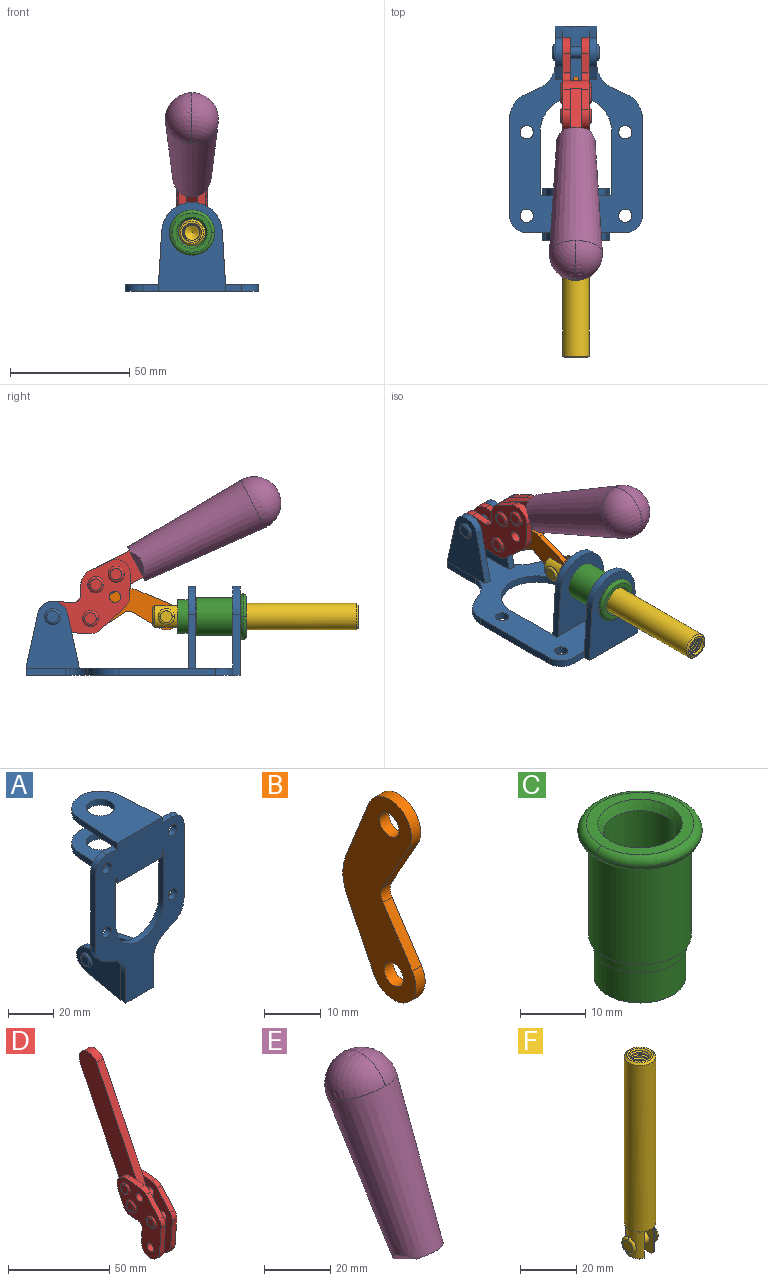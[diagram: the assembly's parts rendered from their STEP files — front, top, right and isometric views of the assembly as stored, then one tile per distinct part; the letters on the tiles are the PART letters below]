
ASSEMBLY  parts=6 mates=6
PART A: 55 faces, bbox 55.7x37.4x89.8 mm
  f0: torus R=2.41mm, axis (-1,0,0), area 15mm2, adj f11,f15,f25
  f1: torus R=2.41mm, axis (-1,0,0), area 15mm2, adj f10,f12,f22
  f2: cylinder r=2.78mm len=5.56mm, axis (0,-1,0), area 54.2mm2, adj f30,f54
  f3: cylinder r=14.99mm len=29.97mm, axis (0,-1,0), area 145.9mm2, adj f30,f49,f53,f54
  f4: cylinder r=2.78mm len=5.56mm, axis (0,-1,0), area 54.2mm2, adj f30,f54
  f5: cylinder r=2.78mm len=5.56mm, axis (0,-1,0), area 54.2mm2, adj f30,f54
  f6: cylinder r=2.78mm len=5.56mm, axis (0,-1,0), area 54.2mm2, adj f30,f54
  f7: cylinder r=6.35mm len=12.7mm, axis (0,0,1), area 123.6mm2, adj f27,f51
  f8: cylinder r=6.35mm len=12.7mm, axis (0,0,-1), area 124.7mm2, adj f21,f35
  f9: cylinder r=2.41mm len=11.18mm, axis (-1,0,0), area 169.4mm2, adj f16,f19
  f10: plane 4.83x4.83mm, normal (1,0,0), area 18.3mm2, adj f1,f12
  f11: plane 4.83x4.83mm, normal (-1,0,0), area 18.3mm2, adj f0,f15
  f12: torus R=2.41mm, axis (-1,0,0), area 15mm2, adj f1,f10,f22
  f13: cylinder r=6.35mm len=12.41mm, axis (1,0,0), area 53.4mm2, adj f18,f19,f22,f23
  f14: cylinder r=6.35mm len=12.41mm, axis (-1,0,0), area 53.4mm2, adj f16,f17,f24,f25
  f15: torus R=2.41mm, axis (-1,0,0), area 15mm2, adj f0,f11,f25
  f16: plane 27.86x22.35mm, normal (1,0,0), area 425.4mm2, adj f9,f14,f17,f24,f30
  f17: plane 22.86x4.97mm, normal (0,0.21,0.98), area 72.5mm2, adj f14,f16,f25,f30
  f18: plane 22.86x4.97mm, normal (0,0.21,0.98), area 72.5mm2, adj f13,f19,f22,f30
  f19: plane 27.86x22.35mm, normal (-1,0,0), area 425.4mm2, adj f9,f13,f18,f23,f30
  f20: cylinder r=12.7mm len=25.35mm, axis (0,0,-1), area 119.8mm2, adj f21,f34,f35,f36
  f21: plane 34.21x28.07mm, normal (0,0,-1), area 702.4mm2, adj f8,f20,f30,f34,f36
  f22: plane 27.96x22.45mm, normal (1,0,0), area 407.2mm2, adj f1,f12,f13,f18,f23,f30,f42,f43
  f23: plane 22.86x4.97mm, normal (0,0.21,-0.98), area 72.5mm2, adj f13,f19,f22,f44
  f24: plane 22.86x4.97mm, normal (0,0.21,-0.98), area 72.5mm2, adj f14,f16,f25,f44
  f25: plane 27.86x22.35mm, normal (-1,0,0), area 407.1mm2, adj f0,f14,f15,f17,f24,f30,f45,f46
  f26: plane 3.1x0.95mm, normal (0,0,-1), area 2.7mm2, adj f30,f49,f50,f54
  f27: plane 34.21x28.07mm, normal (0,0,1), area 702.4mm2, adj f7,f28,f30,f50,f52
  f28: cylinder r=12.7mm len=25.35mm, axis (0,0,1), area 118.8mm2, adj f27,f50,f51,f52
  f29: plane 3.1x0.95mm, normal (0,0,-1), area 2.7mm2, adj f30,f52,f53,f54
  f30: plane 86.54x55.63mm, normal (0,1,0), area 2362.9mm2, adj f2,f3,f4,f5,f6,f16,f17,f18
  f31: plane 40.56x3.1mm, normal (-1,0,0), area 125.7mm2, adj f30,f32,f48,f54
  f32: cylinder r=7.11mm len=7.11mm, axis (0,-1,0), area 34.6mm2, adj f30,f31,f33,f54
  f33: plane 6.67x3.1mm, normal (0,0,1), area 20.4mm2, adj f30,f32,f34,f54
  f34: plane 25.39x3.13mm, normal (-1,0.06,0), area 79.5mm2, adj f20,f21,f33,f35,f54
  f35: plane 37.31x28.45mm, normal (0,0,1), area 789.9mm2, adj f8,f20,f34,f36,f54
  f36: plane 25.39x3.13mm, normal (1,0.06,0), area 79.5mm2, adj f20,f21,f35,f37,f54
  f37: plane 6.67x3.1mm, normal (0,0,1), area 20.4mm2, adj f30,f36,f38,f54
  f38: cylinder r=7.11mm len=7.11mm, axis (0,-1,0), area 34.6mm2, adj f30,f37,f39,f54
  f39: plane 40.56x3.1mm, normal (1,0,0), area 125.7mm2, adj f30,f38,f40,f54
  f40: cylinder r=11.18mm len=10.16mm, axis (0,-1,0), area 39.5mm2, adj f30,f39,f41,f54
  f41: plane 6.09x3.1mm, normal (0.42,0,-0.91), area 20.8mm2, adj f30,f40,f42,f54
  f42: cylinder r=11.18mm len=9.41mm, axis (0,-1,0), area 37.2mm2, adj f22,f30,f41,f43,f54
  f43: plane 16.5x3.1mm, normal (1,0,0), area 51.1mm2, adj f22,f42,f44,f54
  f44: plane 17.37x3.1mm, normal (0,0,-1), area 53.8mm2, adj f23,f24,f30,f43,f45,f54
  f45: plane 16.5x3.1mm, normal (-1,0,0), area 51.1mm2, adj f25,f44,f46,f54
  f46: cylinder r=11.18mm len=9.41mm, axis (0,-1,0), area 37.2mm2, adj f25,f30,f45,f47,f54
  f47: plane 6.09x3.1mm, normal (-0.42,0,-0.91), area 20.8mm2, adj f30,f46,f48,f54
  f48: cylinder r=11.18mm len=10.16mm, axis (0,-1,0), area 39.5mm2, adj f30,f31,f47,f54
  f49: plane 26.54x3.1mm, normal (-1,0,0), area 82.3mm2, adj f3,f26,f30,f54
  f50: plane 25.39x3.1mm, normal (1,0.06,0), area 78.8mm2, adj f26,f27,f28,f51,f54
  f51: plane 37.31x28.45mm, normal (0,0,-1), area 789.9mm2, adj f7,f28,f50,f52,f54
  f52: plane 25.39x3.1mm, normal (-1,0.06,0), area 78.8mm2, adj f27,f28,f29,f51,f54
  f53: plane 26.54x3.1mm, normal (1,0,0), area 82.3mm2, adj f3,f29,f30,f54
  f54: plane 89.66x55.63mm, normal (0,-1,0), area 2678.5mm2, adj f2,f3,f4,f5,f6,f26,f29,f31
PART B: 12 faces, bbox 2.3x18.2x42.8 mm
  f0: cylinder r=2.4mm len=4.8mm, axis (1,0,0), area 34.9mm2, adj f4,f11
  f1: cylinder r=10.41mm len=8.47mm, axis (1,0,0), area 20.2mm2, adj f4,f9,f10,f11
  f2: cylinder r=3.05mm len=3.16mm, axis (1,0,0), area 7.7mm2, adj f4,f6,f7,f11
  f3: cylinder r=2.4mm len=4.8mm, axis (1,0,0), area 34.9mm2, adj f4,f11
  f4: plane 42.81x18.23mm, normal (-1,0,0), area 414.1mm2, adj f0,f1,f2,f3,f5,f6,f7,f8
  f5: cylinder r=5.54mm len=10.67mm, axis (1,0,0), area 41.8mm2, adj f4,f6,f10,f11
  f6: plane 11.66x6.53mm, normal (0,-0.87,-0.49), area 30.9mm2, adj f2,f4,f5,f11
  f7: plane 11.17x7.33mm, normal (0,-0.84,0.55), area 30.9mm2, adj f2,f4,f8,f11
  f8: cylinder r=5.54mm len=10.51mm, axis (1,0,0), area 41.8mm2, adj f4,f7,f9,f11
  f9: plane 13.67x6.67mm, normal (0,0.9,-0.44), area 35.1mm2, adj f1,f4,f8,f11
  f10: plane 14.1x5.7mm, normal (0,0.93,0.37), area 35.1mm2, adj f1,f4,f5,f11
  f11: plane 42.81x18.23mm, normal (1,0,0), area 414.1mm2, adj f0,f1,f2,f3,f5,f6,f7,f8
PART C: 15 faces, bbox 20.6x20.6x28.7 mm
  f0: torus R=8.26mm, axis (0,0,1), area 56.8mm2, adj f1,f10,f12
  f1: torus R=8.26mm, axis (0,0,1), area 56.8mm2, adj f0,f6,f13
  f2: cylinder r=5.59mm len=25.91mm, axis (0,0,1), area 909.6mm2, adj f3,f4
  f3: cone r=6.86mm half-angle=45deg, axis (0,0,-1), area 70.2mm2, adj f2,f14
  f4: cone r=6.47mm half-angle=30deg, axis (0,0,1), area 66.7mm2, adj f2,f13
  f5: cylinder r=7.04mm len=14.07mm, axis (0,0,1), area 252.6mm2, adj f11,f14
  f6: torus R=8.26mm, axis (0,0,1), area 56.8mm2, adj f1,f12,f13
  f7: cylinder r=7.16mm len=14.33mm, axis (0,0,1), area 91.5mm2, adj f9,f11
  f8: cylinder r=7.86mm len=18.42mm, axis (0,0,1), area 909.6mm2, adj f9,f10
  f9: plane 15.72x15.72mm, normal (0,0,-1), area 33mm2, adj f7,f8
  f10: plane 16.51x16.51mm, normal (0,0,-1), area 19.9mm2, adj f0,f8,f12
  f11: plane 14.33x14.33mm, normal (0,0,-1), area 5.7mm2, adj f5,f7
  f12: torus R=8.26mm, axis (0,0,1), area 56.8mm2, adj f0,f6,f10
  f13: plane 16.51x16.51mm, normal (0,0,1), area 82.7mm2, adj f1,f4,f6
  f14: plane 14.07x14.07mm, normal (0,0,-1), area 7.8mm2, adj f3,f5
PART D: 59 faces, bbox 12.9x60.2x99.6 mm
  f0: torus R=2.39mm, axis (-1,0,0), area 14.9mm2, adj f20,f43,f51
  f1: torus R=2.39mm, axis (-1,0,0), area 14.9mm2, adj f19,f42,f51
  f2: torus R=2.39mm, axis (-1,0,0), area 14.9mm2, adj f18,f35,f51
  f3: torus R=2.39mm, axis (-1,0,0), area 14.9mm2, adj f14,f17,f23
  f4: torus R=2.39mm, axis (-1,0,0), area 14.9mm2, adj f13,f16,f23
  f5: torus R=2.39mm, axis (-1,0,0), area 14.9mm2, adj f12,f15,f23
  f6: cylinder r=2.39mm len=4.78mm, axis (1,0,0), area 46.5mm2, adj f48,f50,f51
  f7: cylinder r=2.39mm len=4.78mm, axis (1,0,0), area 46.5mm2, adj f50,f51
  f8: cylinder r=6.35mm len=12.68mm, axis (1,0,0), area 61.8mm2, adj f38,f39,f50,f51
  f9: cylinder r=2.39mm len=4.78mm, axis (-1,0,0), area 70.5mm2, adj f46,f50
  f10: cylinder r=2.39mm len=4.78mm, axis (-1,0,0), area 46.5mm2, adj f23,f45,f46
  f11: cylinder r=2.39mm len=4.78mm, axis (-1,0,0), area 46.5mm2, adj f23,f46
  f12: plane 4.78x4.78mm, normal (1,0,0), area 17.9mm2, adj f5,f15
  f13: plane 4.78x4.78mm, normal (1,0,0), area 17.9mm2, adj f4,f16
  f14: plane 4.78x4.78mm, normal (1,0,0), area 17.9mm2, adj f3,f17
  f15: torus R=2.39mm, axis (-1,0,0), area 14.9mm2, adj f5,f12,f23
  f16: torus R=2.39mm, axis (-1,0,0), area 14.9mm2, adj f4,f13,f23
  f17: torus R=2.39mm, axis (-1,0,0), area 14.9mm2, adj f3,f14,f23
  f18: plane 4.78x4.78mm, normal (-1,0,0), area 17.9mm2, adj f2,f35
  f19: plane 4.78x4.78mm, normal (-1,0,0), area 17.9mm2, adj f1,f42
  f20: plane 4.78x4.78mm, normal (-1,0,0), area 17.9mm2, adj f0,f43
  f21: plane 2.26x0.2mm, normal (1,0,0), area 0.2mm2, adj f31,f44
  f22: plane 2.26x0.2mm, normal (-1,0,0), area 0.2mm2, adj f41,f44
  f23: plane 39.37x30.77mm, normal (1,0,0), area 565.5mm2, adj f3,f4,f5,f10,f11,f15,f16,f17
  f24: cylinder r=6.1mm len=4.15mm, axis (-1,0,0), area 14.7mm2, adj f23,f25,f32,f46
  f25: plane 10.25x9.01mm, normal (0,-0.75,0.66), area 42.3mm2, adj f23,f24,f26,f46
  f26: cylinder r=6.35mm len=4.64mm, axis (-1,0,0), area 15.6mm2, adj f23,f25,f27,f46
  f27: plane 15.84x3.1mm, normal (0,-1,-0.07), area 49.2mm2, adj f23,f26,f28,f46
  f28: cylinder r=6.35mm len=12.68mm, axis (-1,0,0), area 61.8mm2, adj f23,f27,f29,f46
  f29: plane 8.11x3.1mm, normal (0,1,0.07), area 25.2mm2, adj f23,f28,f30,f46
  f30: cylinder r=3.05mm len=3.25mm, axis (-1,0,0), area 14.8mm2, adj f23,f29,f31,f46
  f31: plane 5.99x3.1mm, normal (0,0.07,-1), area 18.6mm2, adj f21,f23,f30,f44,f46
  f32: plane 9.5x3.1mm, normal (0,-0.07,1), area 29.5mm2, adj f23,f24,f33,f46,f47
  f33: cylinder r=6.1mm len=8.63mm, axis (-1,0,0), area 39.1mm2, adj f23,f32,f34,f47
  f34: plane 8.65x3.96mm, normal (0,0.91,-0.42), area 29.5mm2, adj f23,f33,f44,f47
  f35: torus R=2.39mm, axis (-1,0,0), area 14.9mm2, adj f2,f18,f51
  f36: plane 10.25x9.01mm, normal (0,-0.75,0.66), area 42.3mm2, adj f37,f49,f50,f51
  f37: cylinder r=6.35mm len=4.64mm, axis (1,0,0), area 15.6mm2, adj f36,f38,f50,f51
  f38: plane 15.84x3.1mm, normal (0,-1,-0.07), area 49.2mm2, adj f8,f37,f50,f51
  f39: plane 8.11x3.1mm, normal (0,1,0.07), area 25.2mm2, adj f8,f40,f50,f51
  f40: cylinder r=3.05mm len=3.25mm, axis (1,0,0), area 14.8mm2, adj f39,f41,f50,f51
  f41: plane 5.99x3.1mm, normal (0,0.07,-1), area 18.6mm2, adj f22,f40,f44,f50,f51
  f42: torus R=2.39mm, axis (-1,0,0), area 14.9mm2, adj f1,f19,f51
  f43: torus R=2.39mm, axis (-1,0,0), area 14.9mm2, adj f0,f20,f51
  f44: cylinder r=6.35mm len=12.12mm, axis (-1,0,0), area 128.9mm2, adj f21,f22,f23,f31,f34,f41,f46,f47
  f45: plane 2.65x1.35mm, normal (1,0,0), area 1mm2, adj f10,f55
  f46: plane 39.08x20.42mm, normal (-1,0,0), area 412.5mm2, adj f9,f10,f11,f24,f25,f26,f27,f28
  f47: plane 77.62x39.82mm, normal (1,0,0), area 850mm2, adj f32,f33,f34,f44,f53,f54,f55
  f48: plane 2.65x1.35mm, normal (-1,0,0), area 1mm2, adj f6,f55
  f49: cylinder r=6.1mm len=4.15mm, axis (1,0,0), area 14.7mm2, adj f36,f50,f51,f56
  f50: plane 39.08x20.42mm, normal (1,0,0), area 412.5mm2, adj f6,f7,f8,f9,f36,f37,f38,f39
  f51: plane 39.37x30.77mm, normal (-1,0,0), area 565.5mm2, adj f0,f1,f2,f6,f7,f8,f35,f36
  f52: plane 8.65x3.96mm, normal (0,0.91,-0.42), area 29.5mm2, adj f44,f51,f57,f58
  f53: plane 68.49x33.4mm, normal (0,0.9,-0.44), area 358.1mm2, adj f44,f47,f54,f58
  f54: cylinder r=6.35mm len=12.06mm, axis (1,0,0), area 93.7mm2, adj f47,f53,f55,f58
  f55: plane 68.49x33.4mm, normal (0,-0.9,0.44), area 358.1mm2, adj f44,f45,f46,f47,f48,f50,f54,f58
  f56: plane 9.5x3.1mm, normal (0,-0.07,1), area 29.5mm2, adj f49,f50,f51,f57,f58
  f57: cylinder r=6.1mm len=8.63mm, axis (1,0,0), area 39.1mm2, adj f51,f52,f56,f58
  f58: plane 77.62x39.82mm, normal (-1,0,0), area 850mm2, adj f44,f52,f53,f54,f55,f56,f57
PART E: 11 faces, bbox 22.3x42.6x64.5 mm
  f0: sphere r=11.13mm, area 411.4mm2, adj f1,f8
  f1: cone r=11.11mm half-angle=3.3deg, axis (0,0.44,0.9), area 3251.8mm2, adj f0,f7,f8,f9,f10
  f2: cylinder r=6.16mm len=11.7mm, axis (1,0,0), area 89.5mm2, adj f3,f4,f5,f6
  f3: plane 60.23x36.75mm, normal (-1,0,0), area 763.6mm2, adj f2,f4,f6,f10
  f4: plane 51.37x25.05mm, normal (0,0.9,-0.44), area 264.2mm2, adj f2,f3,f5,f10
  f5: plane 60.23x36.75mm, normal (1,0,0), area 763.6mm2, adj f2,f4,f6,f10
  f6: plane 51.37x25.05mm, normal (0,-0.9,0.44), area 264.2mm2, adj f2,f3,f5,f10
  f7: plane 9.95x5.95mm, normal (0.71,-0.31,-0.64), area 25.8mm2, adj f1,f10
  f8: sphere r=11.13mm, area 411.4mm2, adj f0,f1
  f9: plane 9.95x5.95mm, normal (-0.71,-0.31,-0.64), area 25.8mm2, adj f1,f10
  f10: plane 14.27x11.38mm, normal (0,-0.44,-0.9), area 106.7mm2, adj f1,f3,f4,f5,f6,f7,f9
PART F: 48 faces, bbox 12.6x11.1x86.1 mm
  f0: torus R=2.41mm, axis (-1,0,0), area 15mm2, adj f30,f32,f34
  f1: torus R=2.41mm, axis (-1,0,0), area 15mm2, adj f29,f31,f33
  f2: cylinder r=5.54mm len=72.39mm, axis (0,0,1), area 2518.5mm2, adj f3,f4,f42,f43
  f3: cone r=5.54mm half-angle=45deg, axis (0,0,1), area 7.6mm2, adj f2,f5,f41
  f4: cone r=5.54mm half-angle=45deg, axis (0,0,-1), area 34.9mm2, adj f2,f39
  f5: cylinder r=5.08mm len=11.48mm, axis (0,0,1), area 108.3mm2, adj f3,f7,f8,f41
  f6: cylinder r=2.41mm len=4.83mm, axis (-1,0,0), area 71.2mm2, adj f40,f41
  f7: cylinder r=2.41mm len=4.83mm, axis (-1,0,0), area 7.6mm2, adj f5,f34
  f8: cone r=5.08mm half-angle=45deg, axis (0,0,1), area 10.6mm2, adj f5,f37,f41
  f9: cone r=3.98mm half-angle=45deg, axis (0,0,1), area 17.6mm2, adj f27,f39,f45,f46,f47
  f10: cylinder r=2.41mm len=4.83mm, axis (-1,0,0), area 7.6mm2, adj f33,f38
  f11: cylinder r=3.2mm len=6.4mm, axis (0,0,1), area 78.4mm2, adj f12,f28,f44,f45,f47
  f12: cylinder r=3.2mm len=6.4mm, axis (0,0,1), area 10.5mm2, adj f11,f13,f45,f47
  f13: cylinder r=3.2mm len=6.4mm, axis (0,0,1), area 10.5mm2, adj f12,f14,f45,f47
  f14: cylinder r=3.2mm len=6.4mm, axis (0,0,1), area 10.5mm2, adj f13,f15,f45,f47
  f15: cylinder r=3.2mm len=6.4mm, axis (0,0,1), area 10.5mm2, adj f14,f16,f45,f47
  f16: cylinder r=3.2mm len=6.4mm, axis (0,0,1), area 10.5mm2, adj f15,f17,f45,f47
  f17: cylinder r=3.2mm len=6.4mm, axis (0,0,1), area 10.5mm2, adj f16,f18,f45,f47
  f18: cylinder r=3.2mm len=6.4mm, axis (0,0,1), area 10.5mm2, adj f17,f19,f45,f47
  f19: cylinder r=3.2mm len=6.4mm, axis (0,0,1), area 10.5mm2, adj f18,f20,f45,f47
  f20: cylinder r=3.2mm len=6.4mm, axis (0,0,1), area 10.5mm2, adj f19,f21,f45,f47
  f21: cylinder r=3.2mm len=6.4mm, axis (0,0,1), area 10.5mm2, adj f20,f22,f45,f47
  f22: cylinder r=3.2mm len=6.4mm, axis (0,0,1), area 10.5mm2, adj f21,f23,f45,f47
  f23: cylinder r=3.2mm len=6.4mm, axis (0,0,1), area 10.5mm2, adj f22,f24,f45,f47
  f24: cylinder r=3.2mm len=6.4mm, axis (0,0,1), area 10.5mm2, adj f23,f25,f45,f47
  f25: cylinder r=3.2mm len=6.4mm, axis (0,0,1), area 10.5mm2, adj f24,f26,f45,f47
  f26: cylinder r=3.2mm len=6.4mm, axis (0,0,1), area 10.5mm2, adj f25,f27,f45,f47
  f27: cylinder r=3.2mm len=6.4mm, axis (0,0,1), area 7.4mm2, adj f9,f26,f45,f47
  f28: cone r=3.2mm half-angle=60deg, axis (0,0,1), area 37.2mm2, adj f11
  f29: plane 4.83x4.83mm, normal (-1,0,0), area 18.3mm2, adj f1,f31
  f30: plane 4.83x4.83mm, normal (1,0,0), area 18.3mm2, adj f0,f32
  f31: torus R=2.41mm, axis (-1,0,0), area 15mm2, adj f1,f29,f33
  f32: torus R=2.41mm, axis (-1,0,0), area 15mm2, adj f0,f30,f34
  f33: plane 6.83x6.83mm, normal (1,0,0), area 18.3mm2, adj f1,f10,f31
  f34: plane 6.83x6.83mm, normal (-1,0,0), area 18.3mm2, adj f0,f7,f32
  f35: cone r=5.08mm half-angle=45deg, axis (0,0,1), area 10.6mm2, adj f36,f38,f40
  f36: plane 7.25x1.97mm, normal (0,0,-1), area 10mm2, adj f35,f40
  f37: plane 7.25x1.97mm, normal (0,0,-1), area 10mm2, adj f8,f41
  f38: cylinder r=5.08mm len=11.48mm, axis (0,0,1), area 108.3mm2, adj f10,f35,f40,f42
  f39: plane 9.55x9.55mm, normal (0,0,1), area 22mm2, adj f4,f9
  f40: plane 12.76x10.09mm, normal (1,0,0), area 95.7mm2, adj f6,f35,f36,f38,f42,f43
  f41: plane 12.76x10.09mm, normal (-1,0,0), area 95.7mm2, adj f3,f5,f6,f8,f37,f43
  f42: cone r=5.54mm half-angle=45deg, axis (0,0,1), area 7.6mm2, adj f2,f38,f40
  f43: plane 11.07x4.7mm, normal (0,0,-1), area 50.4mm2, adj f2,f40,f41
  f44: plane 0.89x0.62mm, normal (-1,0,0), area 0.3mm2, adj f11,f45,f46,f47
  f45: bspline ~24.8x7.63mm, area 266.6mm2, adj f9,f11,f12,f13,f14,f15,f16,f17
  f46: bspline ~24.87x7.63mm, area 73.6mm2, adj f9,f44,f45,f47
  f47: bspline ~24.98x7.63mm, area 272.5mm2, adj f9,f11,f12,f13,f14,f15,f16,f17
PLACE A rot(axis=(1,0,0),90deg) t=(0,9.43,0)mm fixed
PLACE B rot(axis=(1,0,0),90.6deg) t=(0,9.66,0.17)mm
PLACE C rot(axis=(1,0,0),90deg) t=(0,9.43,0)mm
PLACE D rot(axis=(1,0,0),88.8deg) t=(0,8.91,0.69)mm
PLACE E rot(axis=(1,0,0),88.8deg) t=(-0.04,8.91,0.69)mm
PLACE F rot(axis=(1,0,0),90deg) t=(0,9.4,0)mm
MATE fastened E.f2 <-> D.f54  axis (1,0,0) through (-2.35,-44.34,72.87)mm
MATE revolute D.f4 <-> B.f3  axis (-1,0,0) through (0,25.67,23.84)mm
MATE slider F.f2 <-> C.f12  axis (0,-1,0) through (0,-49.38,24.61)mm
MATE fastened A.f7 <-> C.f2  axis (0,-1,0) through (0,-36.96,24.61)mm
MATE revolute F.f6 <-> B.f5  axis (-1,0,0) through (0,-6.07,24.61)mm
MATE revolute D.f7 <-> A.f0  axis (-1,0,0) through (0,41.52,24.61)mm
